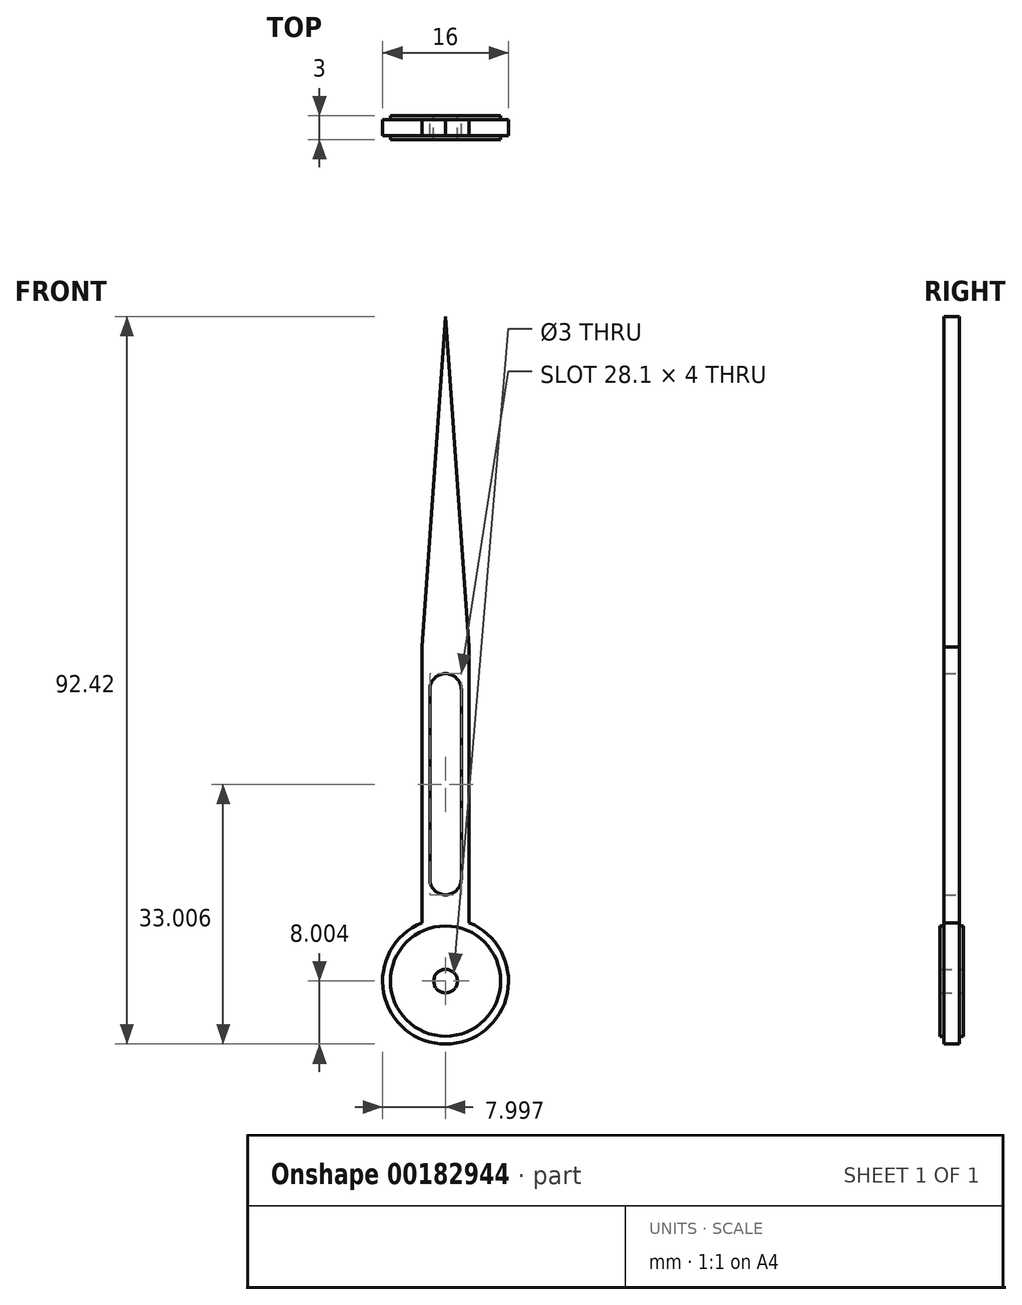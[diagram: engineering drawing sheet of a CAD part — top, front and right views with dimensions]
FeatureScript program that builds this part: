
annotation { "Feature Type Name" : "Feature", "Feature Type Description" : "" }
export const myFeature = defineFeature(function(context is Context, id is Id, definition is map)
    precondition{}
    {
        {
            var Q0;
            Q0=qCreatedBy(makeId("Front.planeOp"),FACE);
            var sketch = newSketch(context, id + "F0", { "sketchPlane" : qUnion([Q0])});
            skCircle(sketch, "E0", {"center": v(-19.83, -33.1) * mm, "radius": 1.5 * mm});
            skCircle(sketch, "E1", {"center": v(-19.83, -33.1) * mm, "radius": 7 * mm});
            skArc(sketch, "E2", {"start": v(-17.83, 3.95) * mm, "mid": v(-19.83, 5.95) * mm, "end": v(-21.83, 3.95) * mm});
            skLineSegment(sketch, "E3.MirrorCS", {"start": v(-16.83, -25.7) * mm, "end": v(-16.83, 9.3) * mm});
            skArc(sketch, "E4", {"start": v(-22.83, -25.7) * mm, "mid": v(-19.83, -41.1) * mm, "end": v(-16.83, -25.7) * mm});
            skArc(sketch, "E5", {"start": v(-21.83, -20.15) * mm, "mid": v(-19.83, -22.15) * mm, "end": v(-17.83, -20.15) * mm});
            skLineSegment(sketch, "E6", {"start": v(-21.83, 3.95) * mm, "end": v(-21.83, -20.15) * mm});
            skLineSegment(sketch, "E7", {"start": v(-17.83, -20.15) * mm, "end": v(-17.83, 3.95) * mm});
            skLineSegment(sketch, "E8.MirrorCS", {"start": v(-22.83, -25.7) * mm, "end": v(-22.83, 9.3) * mm});
            skPoint(sketch, "E9.start.orphan", {"position": v(-19.83, 9.3) * mm});
            skPoint(sketch, "E10.orphan", {"position": v(-22.83, 9.3) * mm});
            skLineSegment(sketch, "E11", {"start": v(-22.83, 9.3) * mm, "end": v(-19.83, 51.3) * mm});
            skLineSegment(sketch, "E12", {"start": v(-16.83, 9.3) * mm, "end": v(-19.83, 51.3) * mm});
            skSolve(sketch);
        }
        {
            var Q0;
            Q0=makeQuery(id+"F0.imprint","IMPRINT",FACE,{"disambiguationData":[TD([[makeQuery(id+"F0.imprint","IMPRINT",EDGE,{"derivedFrom":sQuery(id+"F0.wireOp",EDGE,"E0")}),-1.0]])]});
            var Q1;
            Q1=sQuery(id+"F0.wireOp",EDGE,"p5VHldXC-XaDy-Jo6Q-gzRM-BKwmdG1nrnMR");
            var Q2;
            Q2=sQuery(id+"F0.wireOp",EDGE,"WyDkhZpA-9s04-8oUv-ohR5-d8g4u36zodpv");
            var Q3;
            Q3=sQuery(id+"F0.wireOp",EDGE,"zPygVgP6-IXea-uzZJ-7nVa-Sz4MqIU0xlYZ");
            extrude(context, id + "F1", {"entities" : qUnion([Q0]), "surfaceEntities" : qUnion([Q1, Q2, Q3]), "endBound" : BoundingType.SYMMETRIC, "depth" : 3 * mm});
        }
        {
            var Q0;
            Q0=makeQuery(id+"F0.imprint","IMPRINT",FACE,{"disambiguationData":[TD([[makeQuery(id+"F0.imprint","IMPRINT",EDGE,{"derivedFrom":sQuery(id+"F0.wireOp",EDGE,"64VVkBTR-3lK9-xNKO-ebiv-tDq6J559YHrB.left")}),-1.0]])]});
            var Q1;
            {var subQ4=sQuery(id+"F0.wireOp",EDGE,"lu1gW57d-0Vzo-OwP6-eww9-Gga1czUeg3AM.left");Q1=makeQuery(id+"F0.imprint","IMPRINT",FACE,{"disambiguationData":[TD([[makeQuery(id+"F0.imprint","IMPRINT",EDGE,{"derivedFrom":subQ4}),-1.0]])]});}
            var Q2;
            Q2=makeQuery(id+"F0.imprint","IMPRINT",FACE,{"disambiguationData":[TD([[makeQuery(id+"F0.imprint","IMPRINT",EDGE,{"derivedFrom":sQuery(id+"F0.wireOp",EDGE,"E1")}),-1.0]])]});
            extrude(context, id + "F2", {"entities" : qUnion([Q0, Q1, Q2]), "operationType" : NewBodyOperationType.ADD, "endBound" : BoundingType.SYMMETRIC, "depth" : 2 * mm});
        }
    });
